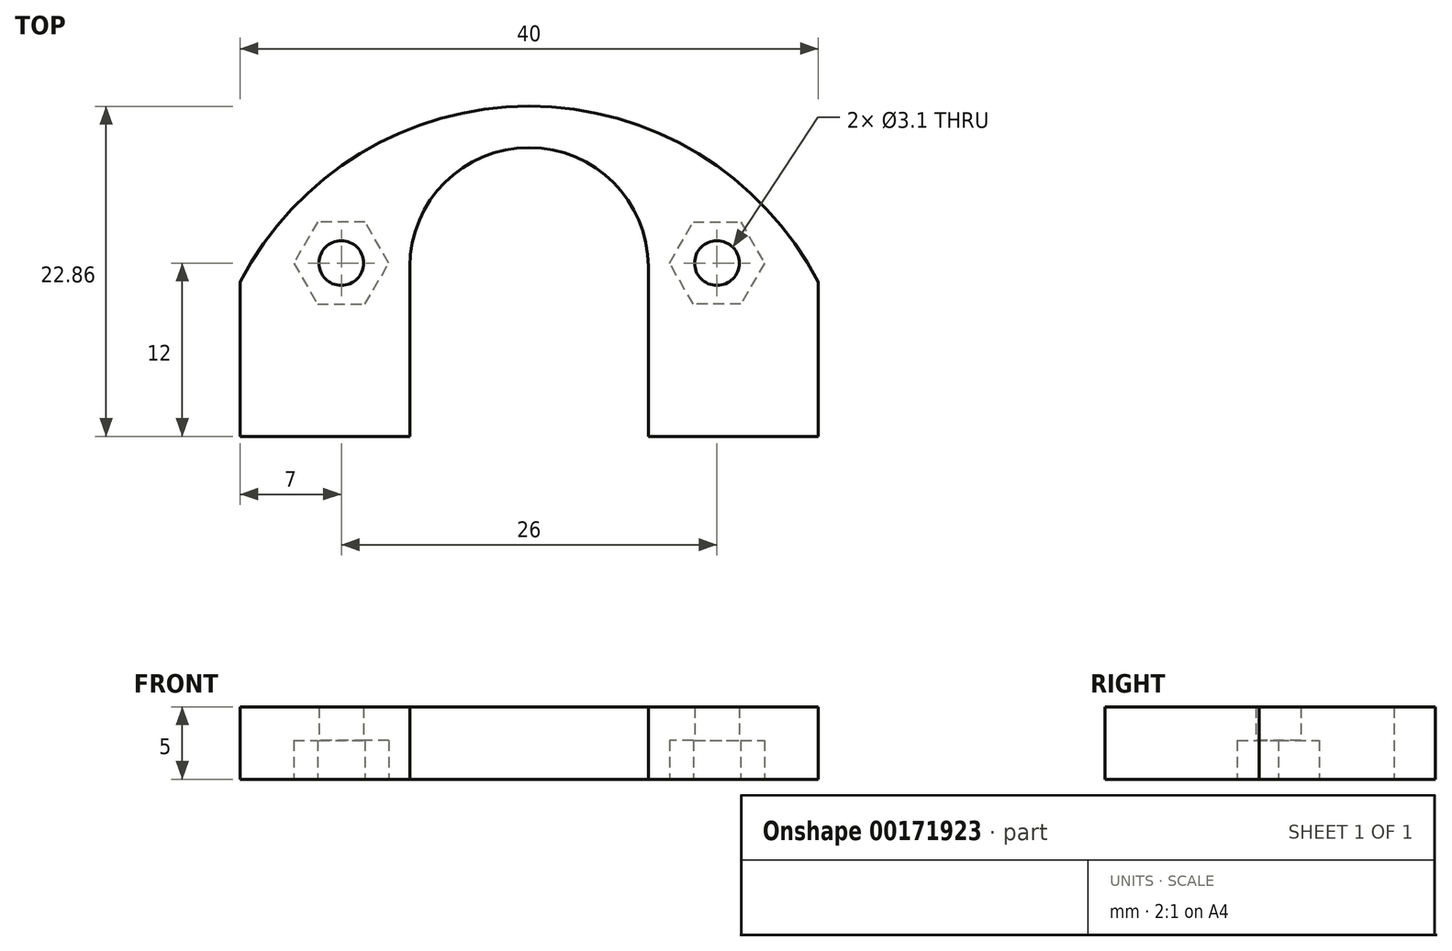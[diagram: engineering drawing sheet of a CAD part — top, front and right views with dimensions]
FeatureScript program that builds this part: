
annotation { "Feature Type Name" : "Feature", "Feature Type Description" : "" }
export const myFeature = defineFeature(function(context is Context, id is Id, definition is map)
    precondition{}
    {
        {
            var Q0;
            Q0=qCreatedBy(makeId("Top.planeOp"),FACE);
            var sketch = newSketch(context, id + "F0", { "sketchPlane" : qUnion([Q0])});
            skLineSegment(sketch, "E0.bottom", {"start": v(-27, 42.5) * mm, "end": v(27, 42.5) * mm});
            skLineSegment(sketch, "E0.top", {"start": v(-20, -42.5) * mm, "end": v(-6.1, -42.5) * mm});
            skLineSegment(sketch, "E0.left", {"start": v(-27, 42.5) * mm, "end": v(-27, -26.5) * mm});
            skLineSegment(sketch, "E0.right", {"start": v(27, 42.5) * mm, "end": v(27, -16.5) * mm});
            skPoint(sketch, "E0.middle", {"position": v(0, 0) * mm});
            skLineSegment(sketch, "E1.left", {"start": v(-20, -26.5) * mm, "end": v(-20, -42.5) * mm});
            skLineSegment(sketch, "E1.right", {"start": v(20, -16.5) * mm, "end": v(20, -42.5) * mm});
            skLineSegment(sketch, "E2", {"start": v(-20, -26.5) * mm, "end": v(-27, -26.5) * mm});
            skPoint(sketch, "E3.orphan", {"position": v(-27, -42.5) * mm});
            skLineSegment(sketch, "E4", {"start": v(20, -16.5) * mm, "end": v(27, -16.5) * mm});
            skPoint(sketch, "E5.orphan", {"position": v(27, -42.5) * mm});
            skCircle(sketch, "E6", {"center": v(-20.4, 30.9) * mm, "radius": 2.6 * mm});
            skCircle(sketch, "E7", {"center": v(-20.4, -6.1) * mm, "radius": 2.6 * mm});
            skCircle(sketch, "E8", {"center": v(20.4, 30.9) * mm, "radius": 2.6 * mm});
            skCircle(sketch, "E9.MirrorC", {"center": v(20.4, -6.1) * mm, "radius": 2.6 * mm});
            skLineSegment(sketch, "E10.bottom", {"start": v(-19, 17.5) * mm, "end": v(-12, 17.5) * mm});
            skLineSegment(sketch, "E10.top", {"start": v(-19, 7.5) * mm, "end": v(-12, 7.5) * mm});
            skLineSegment(sketch, "E10.left", {"start": v(-19, 17.5) * mm, "end": v(-19, 7.5) * mm});
            skLineSegment(sketch, "E10.right", {"start": v(-12, 17.5) * mm, "end": v(-12, 7.5) * mm});
            skLineSegment(sketch, "E11.MirrorCS", {"start": v(12, 17.5) * mm, "end": v(12, 7.5) * mm});
            skLineSegment(sketch, "E12.MirrorCS", {"start": v(19, 7.5) * mm, "end": v(12, 7.5) * mm});
            skLineSegment(sketch, "E13.MirrorCS", {"start": v(19, 17.5) * mm, "end": v(19, 7.5) * mm});
            skLineSegment(sketch, "E14.MirrorCS", {"start": v(19, 17.5) * mm, "end": v(12, 17.5) * mm});
            skEllipse(sketch, "E15", {"center": v(0, -13) * mm, "majorRadius": 7.5 * mm, "minorRadius": 4.5 * mm, "majorAxis": v(1, 0)});
            skArc(sketch, "E16", {"start": v(6.1, -28.75) * mm, "mid": v(0, -22.65) * mm, "end": v(-6.1, -28.75) * mm});
            skCircle(sketch, "E17", {"center": v(-12.5, -13) * mm, "radius": 2 * mm});
            skLineSegment(sketch, "E18", {"start": v(-6.1, -28.75) * mm, "end": v(-6.1, -42.5) * mm});
            skLineSegment(sketch, "E19", {"start": v(6.1, -28.75) * mm, "end": v(6.1, -42.5) * mm});
            skLineSegment(sketch, "E20.trimOffspring", {"start": v(6.1, -42.5) * mm, "end": v(20, -42.5) * mm});
            skArc(sketch, "E21", {"start": v(6.1, -34.3) * mm, "mid": v(0, -20.5) * mm, "end": v(-6.1, -34.3) * mm});
            skCircle(sketch, "E22", {"center": v(0, -28.75) * mm, "radius": 6 * mm});
            skSolve(sketch);
        }
        {
            var Q0;
            {var subQ0=sQuery(id+"F0.wireOp",EDGE,"E16");Q0=makeQuery(id+"F0.imprint","IMPRINT",FACE,{"disambiguationData":[TD([[makeQuery(id+"F0.imprint","IMPRINT",EDGE,{"derivedFrom":subQ0}),-1.0]])]});}
            var Q1;
            Q1=makeQuery(id+"F0.imprint","IMPRINT",FACE,{"disambiguationData":[TD([[makeQuery(id+"F0.imprint","IMPRINT",EDGE,{"derivedFrom":sQuery(id+"F0.wireOp",EDGE,"E0.bottom")}),-1.0]])]});
            extrude(context, id + "F1", {"entities" : qUnion([Q0, Q1]), "depth" : 8 * mm});
        }
        {
            var Q0;
            {var subQ0=sQuery(id+"F0.wireOp",EDGE,"E16");Q0=makeQuery(id+"F0.imprint","IMPRINT",FACE,{"disambiguationData":[TD([[makeQuery(id+"F0.imprint","IMPRINT",EDGE,{"derivedFrom":subQ0}),-1.0]])]});}
            extrude(context, id + "F2", {"entities" : qUnion([Q0]), "operationType" : NewBodyOperationType.REMOVE, "depth" : 2.6 * mm});
        }
        {
            var Q0;
            Q0=makeQuery(id+"F0.imprint","IMPRINT",FACE,{"disambiguationData":[TD([[makeQuery(id+"F0.imprint","IMPRINT",EDGE,{"derivedFrom":sQuery(id+"F0.wireOp",EDGE,"E22")}),1.0]])]});
            extrude(context, id + "F3", {"entities" : qUnion([Q0]), "depth" : 25 * mm});
        }
        {
            var Q0;
            Q0=qCreatedBy(makeId("Right.planeOp"),FACE);
            var sketch = newSketch(context, id + "F4", { "sketchPlane" : qUnion([Q0])});
            skCircle(sketch, "E23", {"center": v(-36.45, 5.5) * mm, "radius": 1.65 * mm});
            skLineSegment(sketch, "E24", {"start": v(-34.74, 0) * mm, "end": v(-34.74, 1.48) * mm});
            skSolve(sketch);
        }
        {
            var Q0;
            Q0=makeQuery(id+"F4.imprint","IMPRINT",FACE,{"disambiguationData":[TD([[makeQuery(id+"F4.imprint","IMPRINT",EDGE,{"derivedFrom":sQuery(id+"F4.wireOp",EDGE,"E23")}),1.0]])]});
            extrude(context, id + "F5", {"entities" : qUnion([Q0]), "operationType" : NewBodyOperationType.REMOVE, "endBound" : BoundingType.SYMMETRIC, "oppositeDirection" : true, "depth" : 100 * mm});
        }
        {
            var Q0;
            Q0=makeQuery(id+"F1.opExtrude","SWEPT_FACE",FACE,{"disambiguationData":[OSD([sQuery(id+"F0.wireOp",EDGE,"E20.trimOffspring")])]});
            extrude(context, id + "F6", {"entities" : qUnion([Q0]), "operationType" : NewBodyOperationType.ADD, "depth" : 5 * mm});
        }
        {
            var Q0;
            Q0=makeQuery(id+"F1.opExtrude","SWEPT_FACE",FACE,{"disambiguationData":[OSD([sQuery(id+"F0.wireOp",EDGE,"E0.top")])]});
            extrude(context, id + "F7", {"entities" : qUnion([Q0]), "operationType" : NewBodyOperationType.REMOVE, "oppositeDirection" : true, "depth" : 2 * mm});
        }
        {
            var Q0;
            {var subQ0=sQuery(id+"F0.wireOp",EDGE,"E20.trimOffspring");Q0=makeQuery(id+"F6.boolean.opBoolean","MERGE",FACE,{"derivedFrom":[makeQuery(id+"F1.opExtrude","CAP_FACE",FACE,{"disambiguationData":[OSD([sQuery(id+"F0.wireOp",EDGE,"E0.bottom"),sQuery(id+"F0.wireOp",EDGE,"E0.left"),sQuery(id+"F0.wireOp",EDGE,"E0.right"),sQuery(id+"F0.wireOp",EDGE,"E0.top"),sQuery(id+"F0.wireOp",EDGE,"E1.left"),sQuery(id+"F0.wireOp",EDGE,"E1.right"),sQuery(id+"F0.wireOp",EDGE,"E2"),sQuery(id+"F0.wireOp",EDGE,"E4"),sQuery(id+"F0.wireOp",EDGE,"E6"),sQuery(id+"F0.wireOp",EDGE,"E7"),sQuery(id+"F0.wireOp",EDGE,"E8"),sQuery(id+"F0.wireOp",EDGE,"E9.MirrorC"),sQuery(id+"F0.wireOp",EDGE,"E10.bottom"),sQuery(id+"F0.wireOp",EDGE,"E10.top"),sQuery(id+"F0.wireOp",EDGE,"E10.left"),sQuery(id+"F0.wireOp",EDGE,"E10.right"),sQuery(id+"F0.wireOp",EDGE,"E11.MirrorCS"),sQuery(id+"F0.wireOp",EDGE,"E12.MirrorCS"),sQuery(id+"F0.wireOp",EDGE,"E13.MirrorCS"),sQuery(id+"F0.wireOp",EDGE,"E14.MirrorCS"),sQuery(id+"F0.wireOp",EDGE,"E15"),sQuery(id+"F0.wireOp",EDGE,"E16"),sQuery(id+"F0.wireOp",EDGE,"E17"),sQuery(id+"F0.wireOp",EDGE,"E18"),sQuery(id+"F0.wireOp",EDGE,"E19"),subQ0])],"isStart":true}),makeQuery(id+"F6.opExtrude","SWEPT_FACE",FACE,{"disambiguationData":[OSD([subQ0]),TDD([makeQuery(id+"F1.opExtrude","CAP_EDGE",EDGE,{"disambiguationData":[OSD([subQ0])],"isStart":true})])]})]});}
            var sketch = newSketch(context, id + "F8", { "sketchPlane" : qUnion([Q0])});
            skLineSegment(sketch, "E25", {"start": v(8.25, 28.75) * mm, "end": v(8.25, 47.5) * mm});
            skLineSegment(sketch, "E26", {"start": v(-8.25, 28.75) * mm, "end": v(-8.25, 40.5) * mm});
            skLineSegment(sketch, "E27", {"start": v(0, 28.75) * mm, "end": v(8.25, 28.75) * mm});
            skLineSegment(sketch, "E28", {"start": v(0, 28.75) * mm, "end": v(-8.25, 28.75) * mm});
            skSolve(sketch);
        }
        {
            var Q0;
            {var subQ0=sQuery(id+"F8.wireOp",EDGE,"E25");Q0=makeQuery(id+"F8.imprint","IMPRINT",FACE,{"disambiguationData":[TD([[makeQuery(id+"F8.imprint","IMPRINT",EDGE,{"derivedFrom":subQ0}),1.0]])]});}
            var Q1;
            {var subQ0=sQuery(id+"F8.wireOp",EDGE,"E26");Q1=makeQuery(id+"F8.imprint","IMPRINT",FACE,{"disambiguationData":[TD([[makeQuery(id+"F8.imprint","IMPRINT",EDGE,{"derivedFrom":subQ0}),-1.0]])]});}
            var Q2;
            Q2=makeQuery(id+"F2.boolean.opBoolean","COPY",FACE,{"derivedFrom":makeQuery(id+"F2.opExtrude","CAP_FACE",FACE,{"disambiguationData":[OSD([sQuery(id+"F0.wireOp",EDGE,"E16"),sQuery(id+"F0.wireOp",EDGE,"E18"),sQuery(id+"F0.wireOp",EDGE,"E19"),sQuery(id+"F0.wireOp",EDGE,"E21")])],"isStart":false})});
            extrude(context, id + "F9", {"entities" : qUnion([Q0, Q1]), "operationType" : NewBodyOperationType.REMOVE, "endBound" : BoundingType.UP_TO_SURFACE, "oppositeDirection" : true, "endBoundEntityFace" : qUnion([Q2]), "depth" : 25 * mm});
        }
        {
            var Q0;
            {var subQ0=sQuery(id+"F0.wireOp",EDGE,"E19");Q0=makeQuery(id+"F6.boolean.opBoolean","MERGE",FACE,{"derivedFrom":[makeQuery(id+"F1.opExtrude","SWEPT_FACE",FACE,{"disambiguationData":[OSD([subQ0])]}),makeQuery(id+"F6.opExtrude","SWEPT_FACE",FACE,{"disambiguationData":[OSD([subQ0,sQuery(id+"F0.wireOp",EDGE,"E20.trimOffspring")])]})]});}
            var sketch = newSketch(context, id + "F10", { "sketchPlane" : qUnion([Q0])});
            skLineSegment(sketch, "E29.bottom", {"start": v(47.5, 2.6) * mm, "end": v(40.53, 2.6) * mm});
            skLineSegment(sketch, "E29.top", {"start": v(47.5, 8) * mm, "end": v(40.53, 8) * mm});
            skLineSegment(sketch, "E29.left", {"start": v(47.5, 2.6) * mm, "end": v(47.5, 8) * mm});
            skLineSegment(sketch, "E29.right", {"start": v(40.53, 2.6) * mm, "end": v(40.53, 8) * mm});
            skSolve(sketch);
        }
        {
            var Q0;
            Q0=qSketchRegion(id+"F10",true);
            var Q1;
            Q1=makeQuery(id+"F9.boolean.opBoolean","COPY",FACE,{"derivedFrom":makeQuery(id+"F9.opExtrude","SWEPT_FACE",FACE,{"disambiguationData":[OSD([sQuery(id+"F8.wireOp",EDGE,"E25")])]})});
            extrude(context, id + "F11", {"entities" : qUnion([Q0]), "operationType" : NewBodyOperationType.REMOVE, "endBound" : BoundingType.UP_TO_SURFACE, "oppositeDirection" : true, "endBoundEntityFace" : qUnion([Q1]), "depth" : 25 * mm});
        }
        {
            var Q0;
            Q0=makeQuery(id+"F11.boolean.opBoolean","MERGE",FACE,{"derivedFrom":[makeQuery(id+"F9.boolean.opBoolean","COPY",FACE,{"derivedFrom":makeQuery(id+"F9.opExtrude","SWEPT_FACE",FACE,{"disambiguationData":[OSD([sQuery(id+"F8.wireOp",EDGE,"E25")])]})})],"fromTools":[makeQuery(id+"F11.opExtrude","CAP_FACE",FACE,{"disambiguationData":[OSD([sQuery(id+"F10.wireOp",EDGE,"E29.bottom"),sQuery(id+"F10.wireOp",EDGE,"E29.top"),sQuery(id+"F10.wireOp",EDGE,"E29.left"),sQuery(id+"F10.wireOp",EDGE,"E29.right")])],"isStart":false})]});
            var sketch = newSketch(context, id + "F12", { "sketchPlane" : qUnion([Q0])});
            skCircle(sketch, "E30", {"center": v(43.82, 4) * mm, "radius": 1.65 * mm});
            skPoint(sketch, "E30.centerSnap0", {"position": v(47.5, 4) * mm});
            skSolve(sketch);
        }
        {
            var Q0;
            Q0=makeQuery(id+"F12.imprint","IMPRINT",FACE,{"disambiguationData":[TD([[makeQuery(id+"F12.imprint","IMPRINT",EDGE,{"derivedFrom":sQuery(id+"F12.wireOp",EDGE,"E30")}),1.0]])]});
            extrude(context, id + "F13", {"entities" : qUnion([Q0]), "operationType" : NewBodyOperationType.REMOVE, "oppositeDirection" : true, "depth" : 25 * mm});
        }
        {
            var Q0;
            {var subQ0=sQuery(id+"F0.wireOp",EDGE,"E20.trimOffspring");Q0=makeQuery(id+"F6.boolean.opBoolean","MERGE",FACE,{"derivedFrom":[makeQuery(id+"F1.opExtrude","CAP_FACE",FACE,{"disambiguationData":[OSD([sQuery(id+"F0.wireOp",EDGE,"E0.bottom"),sQuery(id+"F0.wireOp",EDGE,"E0.left"),sQuery(id+"F0.wireOp",EDGE,"E0.right"),sQuery(id+"F0.wireOp",EDGE,"E0.top"),sQuery(id+"F0.wireOp",EDGE,"E1.left"),sQuery(id+"F0.wireOp",EDGE,"E1.right"),sQuery(id+"F0.wireOp",EDGE,"E2"),sQuery(id+"F0.wireOp",EDGE,"E4"),sQuery(id+"F0.wireOp",EDGE,"E6"),sQuery(id+"F0.wireOp",EDGE,"E7"),sQuery(id+"F0.wireOp",EDGE,"E8"),sQuery(id+"F0.wireOp",EDGE,"E9.MirrorC"),sQuery(id+"F0.wireOp",EDGE,"E10.bottom"),sQuery(id+"F0.wireOp",EDGE,"E10.top"),sQuery(id+"F0.wireOp",EDGE,"E10.left"),sQuery(id+"F0.wireOp",EDGE,"E10.right"),sQuery(id+"F0.wireOp",EDGE,"E11.MirrorCS"),sQuery(id+"F0.wireOp",EDGE,"E12.MirrorCS"),sQuery(id+"F0.wireOp",EDGE,"E13.MirrorCS"),sQuery(id+"F0.wireOp",EDGE,"E14.MirrorCS"),sQuery(id+"F0.wireOp",EDGE,"E15"),sQuery(id+"F0.wireOp",EDGE,"E16"),sQuery(id+"F0.wireOp",EDGE,"E17"),sQuery(id+"F0.wireOp",EDGE,"E18"),sQuery(id+"F0.wireOp",EDGE,"E19"),subQ0])],"isStart":true}),makeQuery(id+"F6.opExtrude","SWEPT_FACE",FACE,{"disambiguationData":[OSD([subQ0]),TDD([makeQuery(id+"F1.opExtrude","CAP_EDGE",EDGE,{"disambiguationData":[OSD([subQ0])],"isStart":true})])]})]});}
            var sketch = newSketch(context, id + "F14", { "sketchPlane" : qUnion([Q0])});
            skCircle(sketch, "E31.cCircle", {"center": v(-13, 28.5) * mm, "radius": 2.85 * mm, "construction": true});
            skLineSegment(sketch, "E31.0", {"start": v(-11.35, 25.65) * mm, "end": v(-14.65, 25.65) * mm});
            skLineSegment(sketch, "E31.1", {"start": v(-14.65, 25.65) * mm, "end": v(-16.3, 28.5) * mm});
            skLineSegment(sketch, "E31.2", {"start": v(-16.3, 28.5) * mm, "end": v(-14.65, 31.35) * mm});
            skLineSegment(sketch, "E31.3", {"start": v(-14.65, 31.35) * mm, "end": v(-11.35, 31.35) * mm});
            skLineSegment(sketch, "E31.4", {"start": v(-11.35, 31.35) * mm, "end": v(-9.7, 28.5) * mm});
            skLineSegment(sketch, "E31.5", {"start": v(-9.7, 28.5) * mm, "end": v(-11.35, 25.65) * mm});
            skPoint(sketch, "E31.0.midPoint", {"position": v(-13, 25.65) * mm});
            skLineSegment(sketch, "E32.MirrorCS", {"start": v(9.7, 28.5) * mm, "end": v(11.35, 25.65) * mm});
            skLineSegment(sketch, "E33.MirrorCS", {"start": v(11.35, 31.35) * mm, "end": v(9.7, 28.5) * mm});
            skLineSegment(sketch, "E34.MirrorCS", {"start": v(14.65, 31.35) * mm, "end": v(11.35, 31.35) * mm});
            skPoint(sketch, "E35.MirrorP", {"position": v(13, 25.65) * mm});
            skCircle(sketch, "E36.MirrorC", {"center": v(13, 28.5) * mm, "radius": 2.85 * mm, "construction": true});
            skLineSegment(sketch, "E37.MirrorCS", {"start": v(11.35, 25.65) * mm, "end": v(14.65, 25.65) * mm});
            skLineSegment(sketch, "E38.MirrorCS", {"start": v(14.65, 25.65) * mm, "end": v(16.3, 28.5) * mm});
            skLineSegment(sketch, "E39.MirrorCS", {"start": v(16.3, 28.5) * mm, "end": v(14.65, 31.35) * mm});
            skCircle(sketch, "E40", {"center": v(-13, 28.5) * mm, "radius": 1.55 * mm});
            skCircle(sketch, "E41.MirrorC", {"center": v(13, 28.5) * mm, "radius": 1.55 * mm});
            skSolve(sketch);
        }
        {
            var Q0;
            Q0=qSketchRegion(id+"F14",true);
            extrude(context, id + "F15", {"entities" : qUnion([Q0]), "operationType" : NewBodyOperationType.REMOVE, "oppositeDirection" : true, "depth" : 2.7 * mm});
        }
        {
            var Q0;
            {var subQ0=sQuery(id+"F0.wireOp",EDGE,"E20.trimOffspring");Q0=makeQuery(id+"F15.boolean.opBoolean","SPLIT",FACE,{"disambiguationData":[TD([makeQuery(id+"F15.opExtrude","SWEPT_FACE",FACE,{"disambiguationData":[OSD([sQuery(id+"F14.wireOp",EDGE,"E40")])]})])],"derivedFrom":makeQuery(id+"F6.boolean.opBoolean","MERGE",FACE,{"derivedFrom":[makeQuery(id+"F1.opExtrude","CAP_FACE",FACE,{"disambiguationData":[OSD([sQuery(id+"F0.wireOp",EDGE,"E0.bottom"),sQuery(id+"F0.wireOp",EDGE,"E0.left"),sQuery(id+"F0.wireOp",EDGE,"E0.right"),sQuery(id+"F0.wireOp",EDGE,"E0.top"),sQuery(id+"F0.wireOp",EDGE,"E1.left"),sQuery(id+"F0.wireOp",EDGE,"E1.right"),sQuery(id+"F0.wireOp",EDGE,"E2"),sQuery(id+"F0.wireOp",EDGE,"E4"),sQuery(id+"F0.wireOp",EDGE,"E6"),sQuery(id+"F0.wireOp",EDGE,"E7"),sQuery(id+"F0.wireOp",EDGE,"E8"),sQuery(id+"F0.wireOp",EDGE,"E9.MirrorC"),sQuery(id+"F0.wireOp",EDGE,"E10.bottom"),sQuery(id+"F0.wireOp",EDGE,"E10.top"),sQuery(id+"F0.wireOp",EDGE,"E10.left"),sQuery(id+"F0.wireOp",EDGE,"E10.right"),sQuery(id+"F0.wireOp",EDGE,"E11.MirrorCS"),sQuery(id+"F0.wireOp",EDGE,"E12.MirrorCS"),sQuery(id+"F0.wireOp",EDGE,"E13.MirrorCS"),sQuery(id+"F0.wireOp",EDGE,"E14.MirrorCS"),sQuery(id+"F0.wireOp",EDGE,"E15"),sQuery(id+"F0.wireOp",EDGE,"E16"),sQuery(id+"F0.wireOp",EDGE,"E17"),sQuery(id+"F0.wireOp",EDGE,"E18"),sQuery(id+"F0.wireOp",EDGE,"E19"),subQ0])],"isStart":true}),makeQuery(id+"F6.opExtrude","SWEPT_FACE",FACE,{"disambiguationData":[OSD([subQ0]),TDD([makeQuery(id+"F1.opExtrude","CAP_EDGE",EDGE,{"disambiguationData":[OSD([subQ0])],"isStart":true})])]})]})});}
            var Q1;
            {var subQ0=sQuery(id+"F0.wireOp",EDGE,"E20.trimOffspring");Q1=makeQuery(id+"F15.boolean.opBoolean","SPLIT",FACE,{"disambiguationData":[TD([makeQuery(id+"F15.opExtrude","SWEPT_FACE",FACE,{"disambiguationData":[OSD([sQuery(id+"F14.wireOp",EDGE,"E41.MirrorC")])]})])],"derivedFrom":makeQuery(id+"F6.boolean.opBoolean","MERGE",FACE,{"derivedFrom":[makeQuery(id+"F1.opExtrude","CAP_FACE",FACE,{"disambiguationData":[OSD([sQuery(id+"F0.wireOp",EDGE,"E0.bottom"),sQuery(id+"F0.wireOp",EDGE,"E0.left"),sQuery(id+"F0.wireOp",EDGE,"E0.right"),sQuery(id+"F0.wireOp",EDGE,"E0.top"),sQuery(id+"F0.wireOp",EDGE,"E1.left"),sQuery(id+"F0.wireOp",EDGE,"E1.right"),sQuery(id+"F0.wireOp",EDGE,"E2"),sQuery(id+"F0.wireOp",EDGE,"E4"),sQuery(id+"F0.wireOp",EDGE,"E6"),sQuery(id+"F0.wireOp",EDGE,"E7"),sQuery(id+"F0.wireOp",EDGE,"E8"),sQuery(id+"F0.wireOp",EDGE,"E9.MirrorC"),sQuery(id+"F0.wireOp",EDGE,"E10.bottom"),sQuery(id+"F0.wireOp",EDGE,"E10.top"),sQuery(id+"F0.wireOp",EDGE,"E10.left"),sQuery(id+"F0.wireOp",EDGE,"E10.right"),sQuery(id+"F0.wireOp",EDGE,"E11.MirrorCS"),sQuery(id+"F0.wireOp",EDGE,"E12.MirrorCS"),sQuery(id+"F0.wireOp",EDGE,"E13.MirrorCS"),sQuery(id+"F0.wireOp",EDGE,"E14.MirrorCS"),sQuery(id+"F0.wireOp",EDGE,"E15"),sQuery(id+"F0.wireOp",EDGE,"E16"),sQuery(id+"F0.wireOp",EDGE,"E17"),sQuery(id+"F0.wireOp",EDGE,"E18"),sQuery(id+"F0.wireOp",EDGE,"E19"),subQ0])],"isStart":true}),makeQuery(id+"F6.opExtrude","SWEPT_FACE",FACE,{"disambiguationData":[OSD([subQ0]),TDD([makeQuery(id+"F1.opExtrude","CAP_EDGE",EDGE,{"disambiguationData":[OSD([subQ0])],"isStart":true})])]})]})});}
            extrude(context, id + "F16", {"entities" : qUnion([Q0, Q1]), "operationType" : NewBodyOperationType.REMOVE, "oppositeDirection" : true, "depth" : 25 * mm});
        }
        {
            var Q0;
            Q0=makeQuery(id+"F1.opExtrude","SWEPT_EDGE",EDGE,{"disambiguationData":[OSD([sQuery(id+"F0.wireOp",EDGE,"E0.bottom"),sQuery(id+"F0.wireOp",EDGE,"E0.right")])]});
            var Q1;
            Q1=makeQuery(id+"F1.opExtrude","SWEPT_EDGE",EDGE,{"disambiguationData":[OSD([sQuery(id+"F0.wireOp",EDGE,"E0.bottom"),sQuery(id+"F0.wireOp",EDGE,"E0.left")])]});
            var Q2;
            Q2=makeQuery(id+"F1.opExtrude","SWEPT_EDGE",EDGE,{"disambiguationData":[OSD([sQuery(id+"F0.wireOp",EDGE,"E0.left"),sQuery(id+"F0.wireOp",EDGE,"E2")])]});
            var Q3;
            Q3=makeQuery(id+"F1.opExtrude","SWEPT_EDGE",EDGE,{"disambiguationData":[OSD([sQuery(id+"F0.wireOp",EDGE,"E0.right"),sQuery(id+"F0.wireOp",EDGE,"E4")])]});
            fillet(context, id + "F17", {"entities" : qUnion([Q0, Q1, Q2, Q3]), "radius" : 7 * mm, "tangentPropagation" : true, "allowEdgeOverflow" : false});
        }
        {
            var Q0;
            {var subQ0=sQuery(id+"F0.wireOp",EDGE,"E17");var subQ1=sQuery(id+"F0.wireOp",EDGE,"E15");var subQ2=sQuery(id+"F0.wireOp",EDGE,"E14.MirrorCS");var subQ3=sQuery(id+"F0.wireOp",EDGE,"E13.MirrorCS");var subQ4=sQuery(id+"F0.wireOp",EDGE,"E0.right");var subQ5=sQuery(id+"F0.wireOp",EDGE,"E12.MirrorCS");var subQ6=sQuery(id+"F0.wireOp",EDGE,"E11.MirrorCS");var subQ7=sQuery(id+"F0.wireOp",EDGE,"E0.top");var subQ8=sQuery(id+"F0.wireOp",EDGE,"E10.right");var subQ9=sQuery(id+"F0.wireOp",EDGE,"E10.left");var subQ10=sQuery(id+"F0.wireOp",EDGE,"E10.top");var subQ11=sQuery(id+"F0.wireOp",EDGE,"E10.bottom");var subQ12=sQuery(id+"F0.wireOp",EDGE,"E9.MirrorC");var subQ13=sQuery(id+"F0.wireOp",EDGE,"E1.left");var subQ14=sQuery(id+"F0.wireOp",EDGE,"E0.left");var subQ15=sQuery(id+"F0.wireOp",EDGE,"E0.bottom");var subQ16=sQuery(id+"F0.wireOp",EDGE,"E7");var subQ17=sQuery(id+"F0.wireOp",EDGE,"E1.right");var subQ18=sQuery(id+"F0.wireOp",EDGE,"E2");var subQ19=sQuery(id+"F0.wireOp",EDGE,"E4");var subQ20=sQuery(id+"F0.wireOp",EDGE,"E6");var subQ21=sQuery(id+"F0.wireOp",EDGE,"E8");var subQ22=sQuery(id+"F0.wireOp",EDGE,"E20.trimOffspring");Q0=makeQuery(id+"F15.boolean.opBoolean","SPLIT",FACE,{"disambiguationData":[TD([makeQuery(id+"F1.opExtrude","SWEPT_FACE",FACE,{"disambiguationData":[OSD([subQ15])]})])],"derivedFrom":makeQuery(id+"F6.boolean.opBoolean","MERGE",FACE,{"derivedFrom":[makeQuery(id+"F1.opExtrude","CAP_FACE",FACE,{"disambiguationData":[OSD([subQ15,subQ14,subQ4,subQ7,subQ13,subQ17,subQ18,subQ19,subQ20,subQ16,subQ21,subQ12,subQ11,subQ10,subQ9,subQ8,subQ6,subQ5,subQ3,subQ2,subQ1,sQuery(id+"F0.wireOp",EDGE,"E16"),subQ0,sQuery(id+"F0.wireOp",EDGE,"E18"),sQuery(id+"F0.wireOp",EDGE,"E19"),subQ22])],"isStart":true}),makeQuery(id+"F6.opExtrude","SWEPT_FACE",FACE,{"disambiguationData":[OSD([subQ22]),TDD([makeQuery(id+"F1.opExtrude","CAP_EDGE",EDGE,{"disambiguationData":[OSD([subQ22])],"isStart":true})])]})]})});}
            var sketch = newSketch(context, id + "F18", { "sketchPlane" : qUnion([Q0])});
            skLineSegment(sketch, "E42.bottom", {"start": v(8, -32.5) * mm, "end": v(-8, -32.5) * mm});
            skLineSegment(sketch, "E42.top", {"start": v(8, 2.5) * mm, "end": v(-8, 2.5) * mm});
            skLineSegment(sketch, "E42.left", {"start": v(8, -32.5) * mm, "end": v(8, 2.5) * mm});
            skLineSegment(sketch, "E42.right", {"start": v(-8, -32.5) * mm, "end": v(-8, 2.5) * mm});
            skPoint(sketch, "E42.middle", {"position": v(0, -15) * mm});
            skSolve(sketch);
        }
        {
            var Q0;
            Q0=qSketchRegion(id+"F18",true);
            extrude(context, id + "F19", {"entities" : qUnion([Q0]), "operationType" : NewBodyOperationType.REMOVE, "oppositeDirection" : true, "depth" : 25 * mm});
        }
        {
            var Q0;
            Q0=makeQuery(id+"F19.boolean.opBoolean","COPY",FACE,{"derivedFrom":makeQuery(id+"F19.opExtrude","SWEPT_FACE",FACE,{"disambiguationData":[OSD([sQuery(id+"F18.wireOp",EDGE,"E42.right")])]})});
            var sketch = newSketch(context, id + "F20", { "sketchPlane" : qUnion([Q0])});
            skLineSegment(sketch, "E43.bottom", {"start": v(10.5, 8) * mm, "end": v(20.5, 8) * mm});
            skLineSegment(sketch, "E43.top", {"start": v(10.5, 0) * mm, "end": v(20.5, 0) * mm});
            skLineSegment(sketch, "E43.left", {"start": v(10.5, 8) * mm, "end": v(10.5, 0) * mm});
            skLineSegment(sketch, "E43.right", {"start": v(20.5, 8) * mm, "end": v(20.5, 0) * mm});
            skSolve(sketch);
        }
        {
            var Q0;
            Q0=qSketchRegion(id+"F20",true);
            extrude(context, id + "F21", {"entities" : qUnion([Q0]), "operationType" : NewBodyOperationType.ADD, "endBound" : BoundingType.UP_TO_NEXT, "depth" : 25 * mm});
        }
        {
            var Q0;
            Q0=makeQuery(id+"F21.opExtrude","CAP_EDGE",EDGE,{"disambiguationData":[OSD([sQuery(id+"F20.wireOp",EDGE,"E43.left")])],"isStart":true});
            var Q1;
            Q1=makeQuery(id+"F19.boolean.opBoolean","COPY",EDGE,{"derivedFrom":makeQuery(id+"F19.opExtrude","SWEPT_EDGE",EDGE,{"disambiguationData":[OSD([sQuery(id+"F18.wireOp",EDGE,"E42.top"),sQuery(id+"F18.wireOp",EDGE,"E42.right")])]})});
            var Q2;
            Q2=makeQuery(id+"F19.boolean.opBoolean","COPY",EDGE,{"derivedFrom":makeQuery(id+"F19.opExtrude","SWEPT_EDGE",EDGE,{"disambiguationData":[OSD([sQuery(id+"F18.wireOp",EDGE,"E42.top"),sQuery(id+"F18.wireOp",EDGE,"E42.left")])]})});
            var Q3;
            Q3=makeQuery(id+"F21.opExtrude","CAP_EDGE",EDGE,{"disambiguationData":[OSD([sQuery(id+"F20.wireOp",EDGE,"E43.left")])],"isStart":false});
            var Q4;
            Q4=makeQuery(id+"F21.opExtrude","CAP_EDGE",EDGE,{"disambiguationData":[OSD([sQuery(id+"F20.wireOp",EDGE,"E43.right")])],"isStart":false});
            var Q5;
            Q5=makeQuery(id+"F21.opExtrude","CAP_EDGE",EDGE,{"disambiguationData":[OSD([sQuery(id+"F20.wireOp",EDGE,"E43.right")])],"isStart":true});
            var Q6;
            Q6=makeQuery(id+"F19.boolean.opBoolean","COPY",EDGE,{"derivedFrom":makeQuery(id+"F19.opExtrude","SWEPT_EDGE",EDGE,{"disambiguationData":[OSD([sQuery(id+"F18.wireOp",EDGE,"E42.bottom"),sQuery(id+"F18.wireOp",EDGE,"E42.right")])]})});
            var Q7;
            Q7=makeQuery(id+"F19.boolean.opBoolean","COPY",EDGE,{"derivedFrom":makeQuery(id+"F19.opExtrude","SWEPT_EDGE",EDGE,{"disambiguationData":[OSD([sQuery(id+"F18.wireOp",EDGE,"E42.bottom"),sQuery(id+"F18.wireOp",EDGE,"E42.left")])]})});
            fillet(context, id + "F22", {"entities" : qUnion([Q0, Q1, Q2, Q3, Q4, Q5, Q6, Q7]), "radius" : 5 * mm, "tangentPropagation" : true, "allowEdgeOverflow" : false});
        }
        {
            var Q0;
            {var subQ0=sQuery(id+"F0.wireOp",EDGE,"E17");var subQ1=sQuery(id+"F0.wireOp",EDGE,"E15");var subQ2=sQuery(id+"F0.wireOp",EDGE,"E14.MirrorCS");var subQ3=sQuery(id+"F0.wireOp",EDGE,"E13.MirrorCS");var subQ4=sQuery(id+"F0.wireOp",EDGE,"E0.right");var subQ5=sQuery(id+"F0.wireOp",EDGE,"E12.MirrorCS");var subQ6=sQuery(id+"F0.wireOp",EDGE,"E11.MirrorCS");var subQ7=sQuery(id+"F0.wireOp",EDGE,"E0.top");var subQ8=sQuery(id+"F0.wireOp",EDGE,"E10.right");var subQ9=sQuery(id+"F0.wireOp",EDGE,"E10.left");var subQ10=sQuery(id+"F0.wireOp",EDGE,"E10.top");var subQ11=sQuery(id+"F0.wireOp",EDGE,"E10.bottom");var subQ12=sQuery(id+"F0.wireOp",EDGE,"E9.MirrorC");var subQ13=sQuery(id+"F0.wireOp",EDGE,"E1.left");var subQ14=sQuery(id+"F0.wireOp",EDGE,"E0.left");var subQ15=sQuery(id+"F0.wireOp",EDGE,"E0.bottom");var subQ16=sQuery(id+"F0.wireOp",EDGE,"E7");var subQ17=sQuery(id+"F0.wireOp",EDGE,"E1.right");var subQ18=sQuery(id+"F0.wireOp",EDGE,"E2");var subQ19=sQuery(id+"F0.wireOp",EDGE,"E4");var subQ20=sQuery(id+"F0.wireOp",EDGE,"E6");var subQ21=sQuery(id+"F0.wireOp",EDGE,"E8");var subQ22=sQuery(id+"F0.wireOp",EDGE,"E20.trimOffspring");Q0=makeQuery(id+"F21.boolean.opBoolean","MERGE",FACE,{"derivedFrom":[makeQuery(id+"F15.boolean.opBoolean","SPLIT",FACE,{"disambiguationData":[TD([makeQuery(id+"F1.opExtrude","SWEPT_FACE",FACE,{"disambiguationData":[OSD([subQ15])]})])],"derivedFrom":makeQuery(id+"F6.boolean.opBoolean","MERGE",FACE,{"derivedFrom":[makeQuery(id+"F1.opExtrude","CAP_FACE",FACE,{"disambiguationData":[OSD([subQ15,subQ14,subQ4,subQ7,subQ13,subQ17,subQ18,subQ19,subQ20,subQ16,subQ21,subQ12,subQ11,subQ10,subQ9,subQ8,subQ6,subQ5,subQ3,subQ2,subQ1,sQuery(id+"F0.wireOp",EDGE,"E16"),subQ0,sQuery(id+"F0.wireOp",EDGE,"E18"),sQuery(id+"F0.wireOp",EDGE,"E19"),subQ22])],"isStart":true}),makeQuery(id+"F6.opExtrude","SWEPT_FACE",FACE,{"disambiguationData":[OSD([subQ22]),TDD([makeQuery(id+"F1.opExtrude","CAP_EDGE",EDGE,{"disambiguationData":[OSD([subQ22])],"isStart":true})])]})]})}),makeQuery(id+"F21.opExtrude","SWEPT_FACE",FACE,{"disambiguationData":[OSD([sQuery(id+"F20.wireOp",EDGE,"E43.top")])]})]});}
            var sketch = newSketch(context, id + "F23", { "sketchPlane" : qUnion([Q0])});
            skPoint(sketch, "E44.oppositeSnap0", {"position": v(15.5, -7.5) * mm});
            skLineSegment(sketch, "E44.bottom", {"start": v(-15.5, -42.5) * mm, "end": v(15.5, -42.5) * mm});
            skLineSegment(sketch, "E44.top", {"start": v(-15.5, 17.5) * mm, "end": v(15.5, 17.5) * mm});
            skLineSegment(sketch, "E44.left", {"start": v(-15.5, -42.5) * mm, "end": v(-15.5, 17.5) * mm});
            skLineSegment(sketch, "E44.right", {"start": v(15.5, -42.5) * mm, "end": v(15.5, 17.5) * mm});
            skSolve(sketch);
        }
        {
            var Q0;
            Q0=qSketchRegion(id+"F23",true);
            extrude(context, id + "F24", {"entities" : qUnion([Q0]), "operationType" : NewBodyOperationType.REMOVE, "oppositeDirection" : true, "depth" : 4 * mm});
        }
        {
            var Q0;
            Q0=makeQuery(id+"F24.boolean.opBoolean","COPY",FACE,{"derivedFrom":makeQuery(id+"F24.opExtrude","CAP_FACE",FACE,{"disambiguationData":[OSD([sQuery(id+"F23.wireOp",EDGE,"E44.bottom"),sQuery(id+"F23.wireOp",EDGE,"E44.top"),sQuery(id+"F23.wireOp",EDGE,"E44.left"),sQuery(id+"F23.wireOp",EDGE,"E44.right")])],"isStart":false})});
            var sketch = newSketch(context, id + "F25", { "sketchPlane" : qUnion([Q0])});
            skLineSegment(sketch, "E45.bottom", {"start": v(-15.5, 17.5) * mm, "end": v(15.5, 17.5) * mm});
            skLineSegment(sketch, "E45.top", {"start": v(-15.5, 7.5) * mm, "end": v(15.5, 7.5) * mm});
            skLineSegment(sketch, "E45.left", {"start": v(-15.5, 17.5) * mm, "end": v(-15.5, 7.5) * mm});
            skLineSegment(sketch, "E45.right", {"start": v(15.5, 17.5) * mm, "end": v(15.5, 7.5) * mm});
            skSolve(sketch);
        }
        {
            var Q0;
            Q0=qSketchRegion(id+"F25",true);
            extrude(context, id + "F26", {"entities" : qUnion([Q0]), "operationType" : NewBodyOperationType.REMOVE, "oppositeDirection" : true, "depth" : 25 * mm});
        }
        {
            var Q0;
            Q0=makeQuery(id+"F1.opExtrude","CAP_EDGE",EDGE,{"disambiguationData":[OSD([sQuery(id+"F0.wireOp",EDGE,"E10.left")])],"isStart":true});
            var Q1;
            Q1=makeQuery(id+"F1.opExtrude","CAP_EDGE",EDGE,{"disambiguationData":[OSD([sQuery(id+"F0.wireOp",EDGE,"E13.MirrorCS")])],"isStart":true});
            fillet(context, id + "F27", {"entities" : qUnion([Q0, Q1]), "radius" : 5 * mm, "tangentPropagation" : true, "allowEdgeOverflow" : false});
        }
        {
            var Q0;
            {var subQ0=sQuery(id+"F23.wireOp",EDGE,"E44.left");Q0=makeQuery(id+"F24.boolean.opBoolean","COPY",EDGE,{"disambiguationData":[TD([makeQuery(id+"F1.opExtrude","SWEPT_FACE",FACE,{"disambiguationData":[OSD([sQuery(id+"F0.wireOp",EDGE,"E10.top")])]})])],"derivedFrom":makeQuery(id+"F24.opExtrude","CAP_EDGE",EDGE,{"disambiguationData":[OSD([subQ0])],"isStart":false})});}
            var Q1;
            {var subQ0=sQuery(id+"F23.wireOp",EDGE,"E44.right");Q1=makeQuery(id+"F24.boolean.opBoolean","COPY",EDGE,{"disambiguationData":[TD([makeQuery(id+"F1.opExtrude","SWEPT_FACE",FACE,{"disambiguationData":[OSD([sQuery(id+"F0.wireOp",EDGE,"E12.MirrorCS")])]})])],"derivedFrom":makeQuery(id+"F24.opExtrude","CAP_EDGE",EDGE,{"disambiguationData":[OSD([subQ0])],"isStart":false})});}
            fillet(context, id + "F28", {"entities" : qUnion([Q0, Q1]), "radius" : 5 * mm, "tangentPropagation" : true, "allowEdgeOverflow" : false});
        }
        {
            var Q0;
            Q0=makeQuery(id+"F26.boolean.opBoolean","COPY",EDGE,{"derivedFrom":makeQuery(id+"F26.opExtrude","SWEPT_EDGE",EDGE,{"disambiguationData":[OSD([sQuery(id+"F23.wireOp",EDGE,"E44.left"),sQuery(id+"F25.wireOp",EDGE,"E45.top"),sQuery(id+"F25.wireOp",EDGE,"E45.left")])]})});
            var Q1;
            Q1=makeQuery(id+"F26.boolean.opBoolean","COPY",EDGE,{"derivedFrom":makeQuery(id+"F26.opExtrude","SWEPT_EDGE",EDGE,{"disambiguationData":[OSD([sQuery(id+"F23.wireOp",EDGE,"E44.right"),sQuery(id+"F25.wireOp",EDGE,"E45.top"),sQuery(id+"F25.wireOp",EDGE,"E45.right")])]})});
            var Q2;
            Q2=makeQuery(id+"F26.boolean.opBoolean","MERGE",EDGE,{"derivedFrom":[makeQuery(id+"F24.boolean.opBoolean","COPY",EDGE,{"derivedFrom":makeQuery(id+"F24.opExtrude","SWEPT_EDGE",EDGE,{"disambiguationData":[OSD([sQuery(id+"F23.wireOp",EDGE,"E44.top"),sQuery(id+"F23.wireOp",EDGE,"E44.right")])]})}),makeQuery(id+"F26.opExtrude","SWEPT_EDGE",EDGE,{"disambiguationData":[OSD([sQuery(id+"F25.wireOp",EDGE,"E45.bottom"),sQuery(id+"F25.wireOp",EDGE,"E45.right")])]})]});
            var Q3;
            Q3=makeQuery(id+"F26.boolean.opBoolean","MERGE",EDGE,{"derivedFrom":[makeQuery(id+"F24.boolean.opBoolean","COPY",EDGE,{"derivedFrom":makeQuery(id+"F24.opExtrude","SWEPT_EDGE",EDGE,{"disambiguationData":[OSD([sQuery(id+"F23.wireOp",EDGE,"E44.top"),sQuery(id+"F23.wireOp",EDGE,"E44.left")])]})}),makeQuery(id+"F26.opExtrude","SWEPT_EDGE",EDGE,{"disambiguationData":[OSD([sQuery(id+"F25.wireOp",EDGE,"E45.bottom"),sQuery(id+"F25.wireOp",EDGE,"E45.left")])]})]});
            fillet(context, id + "F29", {"entities" : qUnion([Q0, Q1, Q2, Q3]), "radius" : 5 * mm, "tangentPropagation" : true, "allowEdgeOverflow" : false});
        }
        {
            var Q0;
            {var subQ0=sQuery(id+"F0.wireOp",EDGE,"E17");var subQ1=sQuery(id+"F0.wireOp",EDGE,"E15");var subQ2=sQuery(id+"F0.wireOp",EDGE,"E14.MirrorCS");var subQ3=sQuery(id+"F0.wireOp",EDGE,"E13.MirrorCS");var subQ4=sQuery(id+"F0.wireOp",EDGE,"E0.right");var subQ5=sQuery(id+"F0.wireOp",EDGE,"E12.MirrorCS");var subQ6=sQuery(id+"F0.wireOp",EDGE,"E11.MirrorCS");var subQ7=sQuery(id+"F0.wireOp",EDGE,"E0.top");var subQ8=sQuery(id+"F0.wireOp",EDGE,"E10.right");var subQ9=sQuery(id+"F0.wireOp",EDGE,"E10.left");var subQ10=sQuery(id+"F0.wireOp",EDGE,"E10.top");var subQ11=sQuery(id+"F0.wireOp",EDGE,"E10.bottom");var subQ12=sQuery(id+"F0.wireOp",EDGE,"E9.MirrorC");var subQ13=sQuery(id+"F0.wireOp",EDGE,"E1.left");var subQ14=sQuery(id+"F0.wireOp",EDGE,"E0.left");var subQ15=sQuery(id+"F0.wireOp",EDGE,"E0.bottom");var subQ16=sQuery(id+"F0.wireOp",EDGE,"E7");var subQ17=sQuery(id+"F0.wireOp",EDGE,"E1.right");var subQ18=sQuery(id+"F0.wireOp",EDGE,"E2");var subQ19=sQuery(id+"F0.wireOp",EDGE,"E4");var subQ20=sQuery(id+"F0.wireOp",EDGE,"E6");var subQ21=sQuery(id+"F0.wireOp",EDGE,"E8");var subQ22=sQuery(id+"F0.wireOp",EDGE,"E20.trimOffspring");Q0=makeQuery(id+"F21.boolean.opBoolean","MERGE",FACE,{"derivedFrom":[makeQuery(id+"F15.boolean.opBoolean","SPLIT",FACE,{"disambiguationData":[TD([makeQuery(id+"F1.opExtrude","SWEPT_FACE",FACE,{"disambiguationData":[OSD([subQ15])]})])],"derivedFrom":makeQuery(id+"F6.boolean.opBoolean","MERGE",FACE,{"derivedFrom":[makeQuery(id+"F1.opExtrude","CAP_FACE",FACE,{"disambiguationData":[OSD([subQ15,subQ14,subQ4,subQ7,subQ13,subQ17,subQ18,subQ19,subQ20,subQ16,subQ21,subQ12,subQ11,subQ10,subQ9,subQ8,subQ6,subQ5,subQ3,subQ2,subQ1,sQuery(id+"F0.wireOp",EDGE,"E16"),subQ0,sQuery(id+"F0.wireOp",EDGE,"E18"),sQuery(id+"F0.wireOp",EDGE,"E19"),subQ22])],"isStart":true}),makeQuery(id+"F6.opExtrude","SWEPT_FACE",FACE,{"disambiguationData":[OSD([subQ22]),TDD([makeQuery(id+"F1.opExtrude","CAP_EDGE",EDGE,{"disambiguationData":[OSD([subQ22])],"isStart":true})])]})]})}),makeQuery(id+"F21.opExtrude","SWEPT_FACE",FACE,{"disambiguationData":[OSD([sQuery(id+"F20.wireOp",EDGE,"E43.top")])]})]});}
            var sketch = newSketch(context, id + "F30", { "sketchPlane" : qUnion([Q0])});
            skLineSegment(sketch, "E46.bottom", {"start": v(-20, 26.5) * mm, "end": v(-33.05, 26.5) * mm});
            skLineSegment(sketch, "E46.top", {"start": v(-20, 17.5) * mm, "end": v(-33.05, 17.5) * mm});
            skLineSegment(sketch, "E46.left", {"start": v(-20, 26.5) * mm, "end": v(-20, 17.5) * mm});
            skLineSegment(sketch, "E46.right", {"start": v(-33.05, 26.5) * mm, "end": v(-33.05, 17.5) * mm});
            skSolve(sketch);
        }
        {
            var Q0;
            Q0=qSketchRegion(id+"F30",true);
            extrude(context, id + "F31", {"entities" : qUnion([Q0]), "operationType" : NewBodyOperationType.REMOVE, "oppositeDirection" : true, "depth" : 25 * mm});
        }
        {
            var Q0;
            Q0=makeQuery(id+"F31.boolean.opBoolean","INTERSECT",EDGE,{"derivedFrom":[makeQuery(id+"F1.opExtrude","SWEPT_FACE",FACE,{"disambiguationData":[OSD([sQuery(id+"F0.wireOp",EDGE,"E0.left")])]}),makeQuery(id+"F31.opExtrude","SWEPT_FACE",FACE,{"disambiguationData":[OSD([sQuery(id+"F30.wireOp",EDGE,"E46.top")])]})]});
            fillet(context, id + "F32", {"entities" : qUnion([Q0]), "radius" : 8 * mm, "tangentPropagation" : true, "allowEdgeOverflow" : false});
        }
        {
            var Q0;
            Q0=qCreatedBy(makeId("Top.planeOp"),FACE);
            var sketch = newSketch(context, id + "F33", { "sketchPlane" : qUnion([Q0])});
            skLineSegment(sketch, "E47.bottom", {"start": v(-4.02, -7) * mm, "end": v(3.98, -7) * mm});
            skLineSegment(sketch, "E47.top", {"start": v(-4.02, -18) * mm, "end": v(3.98, -18) * mm});
            skLineSegment(sketch, "E47.left", {"start": v(-4.02, -7) * mm, "end": v(-4.02, -18) * mm});
            skLineSegment(sketch, "E47.right", {"start": v(3.98, -7) * mm, "end": v(3.98, -18) * mm});
            skSolve(sketch);
        }
        {
            var Q0;
            Q0=qSketchRegion(id+"F33",true);
            var Q1;
            {var subQ0=sQuery(id+"F0.wireOp",EDGE,"E20.trimOffspring");Q1=makeQuery(id+"F21.boolean.opBoolean","MERGE",FACE,{"derivedFrom":[makeQuery(id+"F6.boolean.opBoolean","MERGE",FACE,{"derivedFrom":[makeQuery(id+"F1.opExtrude","CAP_FACE",FACE,{"disambiguationData":[OSD([sQuery(id+"F0.wireOp",EDGE,"E0.bottom"),sQuery(id+"F0.wireOp",EDGE,"E0.left"),sQuery(id+"F0.wireOp",EDGE,"E0.right"),sQuery(id+"F0.wireOp",EDGE,"E0.top"),sQuery(id+"F0.wireOp",EDGE,"E1.left"),sQuery(id+"F0.wireOp",EDGE,"E1.right"),sQuery(id+"F0.wireOp",EDGE,"E2"),sQuery(id+"F0.wireOp",EDGE,"E4"),sQuery(id+"F0.wireOp",EDGE,"E6"),sQuery(id+"F0.wireOp",EDGE,"E7"),sQuery(id+"F0.wireOp",EDGE,"E8"),sQuery(id+"F0.wireOp",EDGE,"E9.MirrorC"),sQuery(id+"F0.wireOp",EDGE,"E10.bottom"),sQuery(id+"F0.wireOp",EDGE,"E10.top"),sQuery(id+"F0.wireOp",EDGE,"E10.left"),sQuery(id+"F0.wireOp",EDGE,"E10.right"),sQuery(id+"F0.wireOp",EDGE,"E11.MirrorCS"),sQuery(id+"F0.wireOp",EDGE,"E12.MirrorCS"),sQuery(id+"F0.wireOp",EDGE,"E13.MirrorCS"),sQuery(id+"F0.wireOp",EDGE,"E14.MirrorCS"),sQuery(id+"F0.wireOp",EDGE,"E15"),sQuery(id+"F0.wireOp",EDGE,"E16"),sQuery(id+"F0.wireOp",EDGE,"E17"),sQuery(id+"F0.wireOp",EDGE,"E18"),sQuery(id+"F0.wireOp",EDGE,"E19"),subQ0])],"isStart":false}),makeQuery(id+"F6.opExtrude","SWEPT_FACE",FACE,{"disambiguationData":[OSD([subQ0]),TDD([makeQuery(id+"F1.opExtrude","CAP_EDGE",EDGE,{"disambiguationData":[OSD([subQ0])],"isStart":false})])]})]}),makeQuery(id+"F21.opExtrude","SWEPT_FACE",FACE,{"disambiguationData":[OSD([sQuery(id+"F20.wireOp",EDGE,"E43.bottom")])]})]});}
            extrude(context, id + "F34", {"entities" : qUnion([Q0]), "operationType" : NewBodyOperationType.ADD, "endBound" : BoundingType.UP_TO_SURFACE, "endBoundEntityFace" : qUnion([Q1]), "depth" : 5.1 * mm});
        }
        {
            var Q0;
            Q0=makeQuery(id+"F34.opExtrude","CAP_EDGE",EDGE,{"disambiguationData":[OSD([sQuery(id+"F33.wireOp",EDGE,"E47.bottom")])],"isStart":true});
            fillet(context, id + "F35", {"entities" : qUnion([Q0]), "radius" : 5 * mm, "tangentPropagation" : true, "allowEdgeOverflow" : false});
        }
        {
            var Q0;
            Q0=makeQuery(id+"F34.boolean.opBoolean","INTERSECT",EDGE,{"derivedFrom":[makeQuery(id+"F26.boolean.opBoolean","COPY",FACE,{"derivedFrom":makeQuery(id+"F26.opExtrude","SWEPT_FACE",FACE,{"disambiguationData":[OSD([sQuery(id+"F25.wireOp",EDGE,"E45.top")])]})}),makeQuery(id+"F34.opExtrude","SWEPT_FACE",FACE,{"disambiguationData":[OSD([sQuery(id+"F33.wireOp",EDGE,"E47.right")])]})]});
            var Q1;
            Q1=makeQuery(id+"F34.boolean.opBoolean","INTERSECT",EDGE,{"derivedFrom":[makeQuery(id+"F26.boolean.opBoolean","COPY",FACE,{"derivedFrom":makeQuery(id+"F26.opExtrude","SWEPT_FACE",FACE,{"disambiguationData":[OSD([sQuery(id+"F25.wireOp",EDGE,"E45.top")])]})}),makeQuery(id+"F34.opExtrude","SWEPT_FACE",FACE,{"disambiguationData":[OSD([sQuery(id+"F33.wireOp",EDGE,"E47.left")])]})]});
            fillet(context, id + "F36", {"entities" : qUnion([Q0, Q1]), "radius" : 2 * mm, "tangentPropagation" : true, "allowEdgeOverflow" : false});
        }
        {
            var Q0;
            Q0=makeQuery(id+"F34.boolean.opBoolean","INTERSECT",EDGE,{"derivedFrom":[makeQuery(id+"F26.boolean.opBoolean","MERGE",FACE,{"derivedFrom":[makeQuery(id+"F24.boolean.opBoolean","COPY",FACE,{"derivedFrom":makeQuery(id+"F24.opExtrude","SWEPT_FACE",FACE,{"disambiguationData":[OSD([sQuery(id+"F23.wireOp",EDGE,"E44.top")])]})})],"fromTools":[makeQuery(id+"F26.opExtrude","SWEPT_FACE",FACE,{"disambiguationData":[OSD([sQuery(id+"F25.wireOp",EDGE,"E45.bottom")])]})]}),makeQuery(id+"F34.opExtrude","SWEPT_FACE",FACE,{"disambiguationData":[OSD([sQuery(id+"F33.wireOp",EDGE,"E47.right")])]})]});
            var Q1;
            Q1=makeQuery(id+"F34.boolean.opBoolean","INTERSECT",EDGE,{"derivedFrom":[makeQuery(id+"F26.boolean.opBoolean","MERGE",FACE,{"derivedFrom":[makeQuery(id+"F24.boolean.opBoolean","COPY",FACE,{"derivedFrom":makeQuery(id+"F24.opExtrude","SWEPT_FACE",FACE,{"disambiguationData":[OSD([sQuery(id+"F23.wireOp",EDGE,"E44.top")])]})})],"fromTools":[makeQuery(id+"F26.opExtrude","SWEPT_FACE",FACE,{"disambiguationData":[OSD([sQuery(id+"F25.wireOp",EDGE,"E45.bottom")])]})]}),makeQuery(id+"F34.opExtrude","SWEPT_FACE",FACE,{"disambiguationData":[OSD([sQuery(id+"F33.wireOp",EDGE,"E47.left")])]})]});
            fillet(context, id + "F37", {"entities" : qUnion([Q0, Q1]), "radius" : 2 * mm, "tangentPropagation" : true, "allowEdgeOverflow" : false});
        }
        {
            var Q0;
            {var subQ0=sQuery(id+"F0.wireOp",EDGE,"E20.trimOffspring");Q0=makeQuery(id+"F34.boolean.opBoolean","MERGE",FACE,{"derivedFrom":[makeQuery(id+"F21.boolean.opBoolean","MERGE",FACE,{"derivedFrom":[makeQuery(id+"F6.boolean.opBoolean","MERGE",FACE,{"derivedFrom":[makeQuery(id+"F1.opExtrude","CAP_FACE",FACE,{"disambiguationData":[OSD([sQuery(id+"F0.wireOp",EDGE,"E0.bottom"),sQuery(id+"F0.wireOp",EDGE,"E0.left"),sQuery(id+"F0.wireOp",EDGE,"E0.right"),sQuery(id+"F0.wireOp",EDGE,"E0.top"),sQuery(id+"F0.wireOp",EDGE,"E1.left"),sQuery(id+"F0.wireOp",EDGE,"E1.right"),sQuery(id+"F0.wireOp",EDGE,"E2"),sQuery(id+"F0.wireOp",EDGE,"E4"),sQuery(id+"F0.wireOp",EDGE,"E6"),sQuery(id+"F0.wireOp",EDGE,"E7"),sQuery(id+"F0.wireOp",EDGE,"E8"),sQuery(id+"F0.wireOp",EDGE,"E9.MirrorC"),sQuery(id+"F0.wireOp",EDGE,"E10.bottom"),sQuery(id+"F0.wireOp",EDGE,"E10.top"),sQuery(id+"F0.wireOp",EDGE,"E10.left"),sQuery(id+"F0.wireOp",EDGE,"E10.right"),sQuery(id+"F0.wireOp",EDGE,"E11.MirrorCS"),sQuery(id+"F0.wireOp",EDGE,"E12.MirrorCS"),sQuery(id+"F0.wireOp",EDGE,"E13.MirrorCS"),sQuery(id+"F0.wireOp",EDGE,"E14.MirrorCS"),sQuery(id+"F0.wireOp",EDGE,"E15"),sQuery(id+"F0.wireOp",EDGE,"E16"),sQuery(id+"F0.wireOp",EDGE,"E17"),sQuery(id+"F0.wireOp",EDGE,"E18"),sQuery(id+"F0.wireOp",EDGE,"E19"),subQ0])],"isStart":false}),makeQuery(id+"F6.opExtrude","SWEPT_FACE",FACE,{"disambiguationData":[OSD([subQ0]),TDD([makeQuery(id+"F1.opExtrude","CAP_EDGE",EDGE,{"disambiguationData":[OSD([subQ0])],"isStart":false})])]})]}),makeQuery(id+"F21.opExtrude","SWEPT_FACE",FACE,{"disambiguationData":[OSD([sQuery(id+"F20.wireOp",EDGE,"E43.bottom")])]})]}),makeQuery(id+"F34.opExtrude","CAP_FACE",FACE,{"disambiguationData":[OSD([sQuery(id+"F33.wireOp",EDGE,"E47.bottom"),sQuery(id+"F33.wireOp",EDGE,"E47.top"),sQuery(id+"F33.wireOp",EDGE,"E47.left"),sQuery(id+"F33.wireOp",EDGE,"E47.right")])],"isStart":false})]});}
            var sketch = newSketch(context, id + "F38", { "sketchPlane" : qUnion([Q0])});
            skArc(sketch, "E48", {"start": v(22.5, -40.5) * mm, "mid": v(0, -17.64) * mm, "end": v(-22.5, -40.5) * mm});
            skPoint(sketch, "E49.firstSnap0", {"position": v(-13.05, -40.5) * mm});
            skLineSegment(sketch, "E49.bottom", {"start": v(-32.93, -40.5) * mm, "end": v(-22.5, -40.5) * mm});
            skLineSegment(sketch, "E49.top", {"start": v(-32.93, 50.07) * mm, "end": v(37.63, 50.07) * mm});
            skLineSegment(sketch, "E49.left", {"start": v(-32.93, -40.5) * mm, "end": v(-32.93, 50.07) * mm});
            skLineSegment(sketch, "E49.right", {"start": v(37.63, -40.5) * mm, "end": v(37.63, 50.07) * mm});
            skLineSegment(sketch, "E50.trimOffspring", {"start": v(22.5, -40.5) * mm, "end": v(37.63, -40.5) * mm});
            skSolve(sketch);
        }
        {
            var Q0;
            Q0 = qSketchRegion(id + "F38", true);
            extrude(context, id + "F39", {"entities" : qUnion([Q0]), "operationType" : NewBodyOperationType.REMOVE, "oppositeDirection" : true, "depth" : 25 * mm, "offsetDistance" : 25 * mm});
        }
        {
            var Q0;
            {var subQ0=sQuery(id+"F0.wireOp",EDGE,"E21");var subQ1=sQuery(id+"F0.wireOp",EDGE,"E18");var subQ2=sQuery(id+"F0.wireOp",EDGE,"E19");Q0=makeQuery(id+"F9.boolean.opBoolean","MERGE",FACE,{"derivedFrom":[makeQuery(id+"F2.boolean.opBoolean","COPY",FACE,{"derivedFrom":makeQuery(id+"F2.opExtrude","CAP_FACE",FACE,{"disambiguationData":[OSD([sQuery(id+"F0.wireOp",EDGE,"E16"),subQ1,subQ2,subQ0])],"isStart":false})})],"fromTools":[makeQuery(id+"F9.opExtrude","CAP_FACE",FACE,{"disambiguationData":[OSD([subQ2,sQuery(id+"F0.wireOp",EDGE,"E20.trimOffspring"),subQ0,sQuery(id+"F8.wireOp",EDGE,"E25")])],"isStart":false}),makeQuery(id+"F9.opExtrude","CAP_FACE",FACE,{"disambiguationData":[OSD([sQuery(id+"F0.wireOp",EDGE,"E0.top"),subQ1,subQ0,sQuery(id+"F8.wireOp",EDGE,"E26")])],"isStart":false})]});}
            extrude(context, id + "F40", {"entities" : qUnion([Q0]), "operationType" : NewBodyOperationType.REMOVE, "oppositeDirection" : true, "depth" : 25 * mm, "offsetDistance" : 25 * mm});
        }
        {
            var Q0;
            Q0=makeQuery(id+"F6.opExtrude","CAP_FACE",FACE,{"disambiguationData":[OSD([sQuery(id+"F0.wireOp",EDGE,"E20.trimOffspring")])],"isStart":false});
            var Q1;
            Q1=makeQuery(id+"F7.boolean.opBoolean","COPY",FACE,{"derivedFrom":makeQuery(id+"F7.opExtrude","CAP_FACE",FACE,{"disambiguationData":[OSD([sQuery(id+"F0.wireOp",EDGE,"E0.top")])],"isStart":false})});
            extrude(context, id + "F41", {"entities" : qUnion([Q0]), "operationType" : NewBodyOperationType.REMOVE, "endBound" : BoundingType.UP_TO_SURFACE, "oppositeDirection" : true, "depth" : 25 * mm, "endBoundEntityFace" : qUnion([Q1]), "offsetDistance" : 25 * mm});
        }
        {
            var Q0;
            Q0=makeQuery(id+"F31.boolean.opBoolean","MERGE",FACE,{"derivedFrom":[makeQuery(id+"F1.opExtrude","SWEPT_FACE",FACE,{"disambiguationData":[OSD([sQuery(id+"F0.wireOp",EDGE,"E1.left")])]}),makeQuery(id+"F31.opExtrude","SWEPT_FACE",FACE,{"disambiguationData":[OSD([sQuery(id+"F30.wireOp",EDGE,"E46.left")])]})]});
            var sketch = newSketch(context, id + "F42", { "sketchPlane" : qUnion([Q0])});
            skCircle(sketch, "E51", {"center": v(36.45, 5.5) * mm, "radius": 2 * mm});
            skSolve(sketch);
        }
        {
            var Q0;
            Q0 = qSketchRegion(id + "F42", true);
            var Q1;
            {var subQ0=sQuery(id+"F8.wireOp",EDGE,"E26");Q1=makeQuery(id+"F40.boolean.opBoolean","MERGE",FACE,{"derivedFrom":[makeQuery(id+"F9.boolean.opBoolean","COPY",FACE,{"derivedFrom":makeQuery(id+"F9.opExtrude","SWEPT_FACE",FACE,{"disambiguationData":[OSD([subQ0])]})})],"fromTools":[makeQuery(id+"F40.opExtrude","SWEPT_FACE",FACE,{"disambiguationData":[OSD([subQ0])]})]});}
            extrude(context, id + "F43", {"entities" : qUnion([Q0]), "operationType" : NewBodyOperationType.ADD, "endBound" : BoundingType.UP_TO_SURFACE, "oppositeDirection" : true, "depth" : 25 * mm, "endBoundEntityFace" : qUnion([Q1]), "offsetDistance" : 25 * mm});
        }
        {
            var Q0;
            {var subQ0=sQuery(id+"F0.wireOp",EDGE,"E1.right");Q0=makeQuery(id+"F6.boolean.opBoolean","MERGE",FACE,{"derivedFrom":[makeQuery(id+"F1.opExtrude","SWEPT_FACE",FACE,{"disambiguationData":[OSD([subQ0])]}),makeQuery(id+"F6.opExtrude","SWEPT_FACE",FACE,{"disambiguationData":[OSD([subQ0,sQuery(id+"F0.wireOp",EDGE,"E20.trimOffspring")])]})]});}
            var sketch = newSketch(context, id + "F44", { "sketchPlane" : qUnion([Q0])});
            skCircle(sketch, "E52", {"center": v(-36.45, 5.5) * mm, "radius": 2 * mm});
            skSolve(sketch);
        }
        {
            var Q0;
            Q0 = qSketchRegion(id + "F44", true);
            var Q1;
            {var subQ0=sQuery(id+"F8.wireOp",EDGE,"E25");Q1=makeQuery(id+"F40.boolean.opBoolean","MERGE",FACE,{"derivedFrom":[makeQuery(id+"F11.boolean.opBoolean","MERGE",FACE,{"derivedFrom":[makeQuery(id+"F9.boolean.opBoolean","COPY",FACE,{"derivedFrom":makeQuery(id+"F9.opExtrude","SWEPT_FACE",FACE,{"disambiguationData":[OSD([subQ0])]})})],"fromTools":[makeQuery(id+"F11.opExtrude","CAP_FACE",FACE,{"disambiguationData":[OSD([sQuery(id+"F10.wireOp",EDGE,"E29.bottom"),sQuery(id+"F10.wireOp",EDGE,"E29.top"),sQuery(id+"F10.wireOp",EDGE,"E29.left"),sQuery(id+"F10.wireOp",EDGE,"E29.right")])],"isStart":false})]})],"fromTools":[makeQuery(id+"F40.opExtrude","SWEPT_FACE",FACE,{"disambiguationData":[OSD([subQ0])]})]});}
            extrude(context, id + "F45", {"entities" : qUnion([Q0]), "operationType" : NewBodyOperationType.ADD, "endBound" : BoundingType.UP_TO_SURFACE, "oppositeDirection" : true, "depth" : 25 * mm, "endBoundEntityFace" : qUnion([Q1]), "offsetDistance" : 25 * mm});
        }
        {
            var Q0;
            Q0=makeQuery(id+"F3.opExtrude","SWEPT_BODY",BODY,{"disambiguationData":[OSD([sQuery(id+"F0.wireOp",EDGE,"E22")])]});
            deleteBodies(context, id + "F46", {"entities" : qUnion([Q0])});
        }
        {
            var Q0;
            {var subQ0=sQuery(id+"F0.wireOp",EDGE,"E20.trimOffspring");Q0=makeQuery(id+"F34.boolean.opBoolean","MERGE",FACE,{"derivedFrom":[makeQuery(id+"F21.boolean.opBoolean","MERGE",FACE,{"derivedFrom":[makeQuery(id+"F6.boolean.opBoolean","MERGE",FACE,{"derivedFrom":[makeQuery(id+"F1.opExtrude","CAP_FACE",FACE,{"disambiguationData":[OSD([sQuery(id+"F0.wireOp",EDGE,"E0.bottom"),sQuery(id+"F0.wireOp",EDGE,"E0.left"),sQuery(id+"F0.wireOp",EDGE,"E0.right"),sQuery(id+"F0.wireOp",EDGE,"E0.top"),sQuery(id+"F0.wireOp",EDGE,"E1.left"),sQuery(id+"F0.wireOp",EDGE,"E1.right"),sQuery(id+"F0.wireOp",EDGE,"E2"),sQuery(id+"F0.wireOp",EDGE,"E4"),sQuery(id+"F0.wireOp",EDGE,"E6"),sQuery(id+"F0.wireOp",EDGE,"E7"),sQuery(id+"F0.wireOp",EDGE,"E8"),sQuery(id+"F0.wireOp",EDGE,"E9.MirrorC"),sQuery(id+"F0.wireOp",EDGE,"E10.bottom"),sQuery(id+"F0.wireOp",EDGE,"E10.top"),sQuery(id+"F0.wireOp",EDGE,"E10.left"),sQuery(id+"F0.wireOp",EDGE,"E10.right"),sQuery(id+"F0.wireOp",EDGE,"E11.MirrorCS"),sQuery(id+"F0.wireOp",EDGE,"E12.MirrorCS"),sQuery(id+"F0.wireOp",EDGE,"E13.MirrorCS"),sQuery(id+"F0.wireOp",EDGE,"E14.MirrorCS"),sQuery(id+"F0.wireOp",EDGE,"E15"),sQuery(id+"F0.wireOp",EDGE,"E16"),sQuery(id+"F0.wireOp",EDGE,"E17"),sQuery(id+"F0.wireOp",EDGE,"E18"),sQuery(id+"F0.wireOp",EDGE,"E19"),subQ0])],"isStart":false}),makeQuery(id+"F6.opExtrude","SWEPT_FACE",FACE,{"disambiguationData":[OSD([subQ0]),TDD([makeQuery(id+"F1.opExtrude","CAP_EDGE",EDGE,{"disambiguationData":[OSD([subQ0])],"isStart":false})])]})]}),makeQuery(id+"F21.opExtrude","SWEPT_FACE",FACE,{"disambiguationData":[OSD([sQuery(id+"F20.wireOp",EDGE,"E43.bottom")])]})]}),makeQuery(id+"F34.opExtrude","CAP_FACE",FACE,{"disambiguationData":[OSD([sQuery(id+"F33.wireOp",EDGE,"E47.bottom"),sQuery(id+"F33.wireOp",EDGE,"E47.top"),sQuery(id+"F33.wireOp",EDGE,"E47.left"),sQuery(id+"F33.wireOp",EDGE,"E47.right")])],"isStart":false})]});}
            extrude(context, id + "F47", {"entities" : qUnion([Q0]), "operationType" : NewBodyOperationType.REMOVE, "oppositeDirection" : true, "depth" : 3 * mm, "offsetDistance" : 25 * mm});
        }
    });
